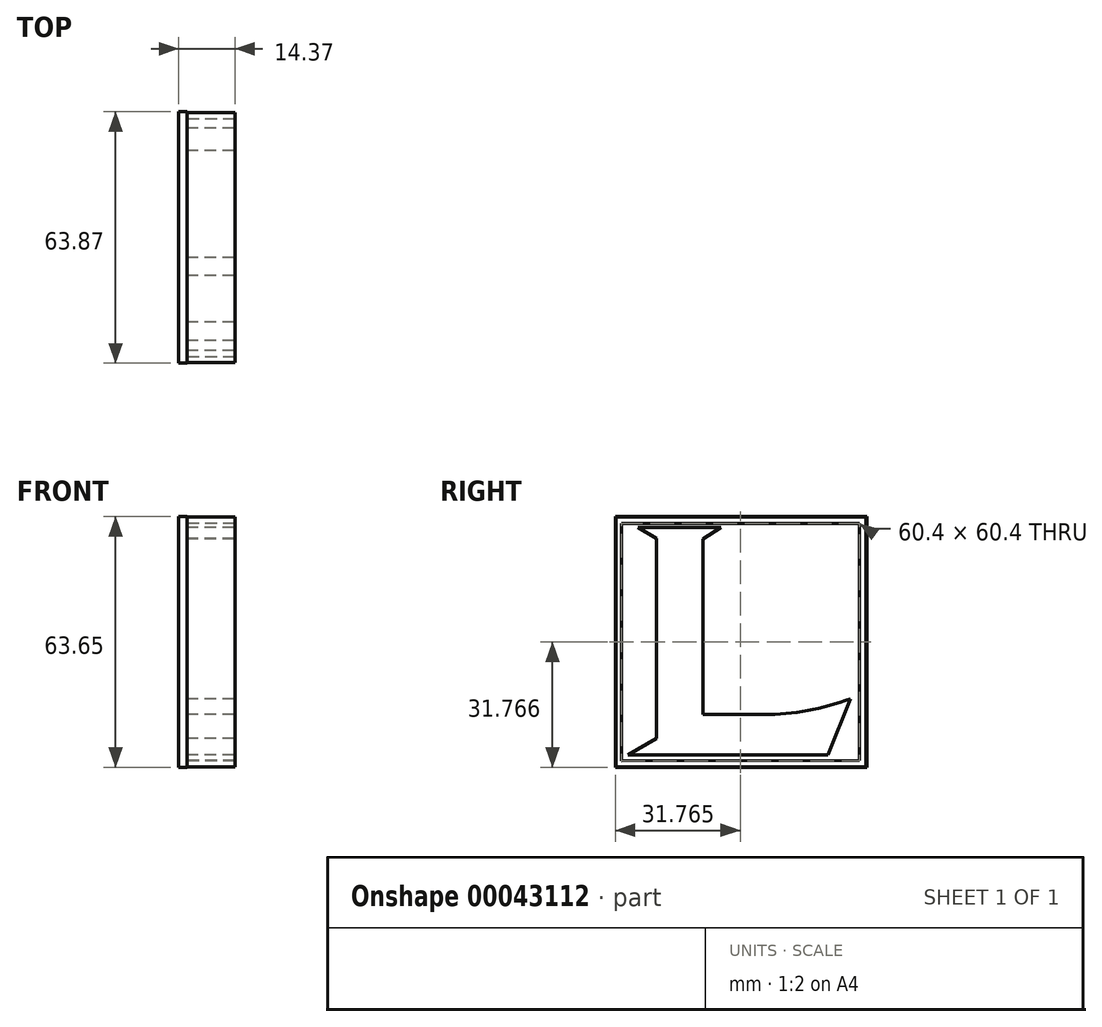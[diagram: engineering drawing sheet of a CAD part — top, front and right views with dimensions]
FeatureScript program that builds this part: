
annotation { "Feature Type Name" : "Feature", "Feature Type Description" : "" }
export const myFeature = defineFeature(function(context is Context, id is Id, definition is map)
    precondition{}
    {
        {
            var Q0;
            Q0=qCreatedBy(makeId("Right.planeOp"),FACE);
            var sketch = newSketch(context, id + "F0", { "sketchPlane" : qUnion([Q0])});
            skLineSegment(sketch, "E0", {"start": v(-7.24, 0) * mm, "end": v(43.56, 0) * mm});
            skLineSegment(sketch, "E1", {"start": v(-7.24, 0) * mm, "end": v(0, 4.13) * mm});
            skLineSegment(sketch, "E2", {"start": v(0, 4.13) * mm, "end": v(0, 54.93) * mm});
            skLineSegment(sketch, "E3", {"start": v(0, 54.93) * mm, "end": v(-4.62, 57.82) * mm});
            skLineSegment(sketch, "E4", {"start": v(-4.62, 57.82) * mm, "end": v(16.37, 57.82) * mm});
            skLineSegment(sketch, "E5", {"start": v(16.37, 57.82) * mm, "end": v(11.85, 54.9) * mm});
            skLineSegment(sketch, "E6", {"start": v(11.85, 54.9) * mm, "end": v(11.85, 10.25) * mm});
            skLineSegment(sketch, "E7", {"start": v(11.85, 10.25) * mm, "end": v(27.27, 10.25) * mm});
            skArc(sketch, "E8", {"start": v(27.27, 10.25) * mm, "mid": v(38.48, 11.25) * mm, "end": v(49.33, 14.23) * mm});
            skLineSegment(sketch, "E9", {"start": v(49.33, 14.23) * mm, "end": v(43.56, 0) * mm});
            skLineSegment(sketch, "E10", {"start": v(-4.62, 57.82) * mm, "end": v(-32.7, 57.82) * mm, "construction": true});
            skLineSegment(sketch, "E11", {"start": v(-32.7, 57.82) * mm, "end": v(-32.7, 0) * mm, "construction": true});
            skLineSegment(sketch, "E12", {"start": v(49.33, 14.23) * mm, "end": v(49.33, -22.32) * mm, "construction": true});
            skLineSegment(sketch, "E13", {"start": v(-7.24, 0) * mm, "end": v(-7.24, -22.1) * mm, "construction": true});
            skLineSegment(sketch, "E14", {"start": v(-7.24, -22.1) * mm, "end": v(49.33, -22.32) * mm, "construction": true});
            skSolve(sketch);
        }
        {
            var Q0;
            Q0=makeQuery(id+"F0.imprint","IMPRINT",FACE,{"disambiguationData":[TD([[makeQuery(id+"F0.imprint","IMPRINT",EDGE,{"derivedFrom":sQuery(id+"F0.wireOp",EDGE,"E0")}),1.0]])]});
            extrude(context, id + "F1", {"entities" : qUnion([Q0]), "depth" : 12.06 * mm});
        }
        {
            var Q0;
            Q0=qCreatedBy(makeId("Right.planeOp"),FACE);
            var sketch = newSketch(context, id + "F2", { "sketchPlane" : qUnion([Q0])});
            skLineSegment(sketch, "E15", {"start": v(-10.25, -3.03) * mm, "end": v(53.25, -3.03) * mm});
            skLineSegment(sketch, "E16", {"start": v(53.25, -3.03) * mm, "end": v(53.25, 60.47) * mm});
            skLineSegment(sketch, "E17", {"start": v(53.25, 60.47) * mm, "end": v(-10.25, 60.47) * mm});
            skLineSegment(sketch, "E18", {"start": v(-10.25, 60.47) * mm, "end": v(-10.25, -3.03) * mm});
            skLineSegment(sketch, "E19", {"start": v(-8.85, -1.59) * mm, "end": v(-8.85, 58.82) * mm});
            skLineSegment(sketch, "E20", {"start": v(-8.85, 58.82) * mm, "end": v(51.56, 58.82) * mm});
            skLineSegment(sketch, "E21", {"start": v(51.56, 58.82) * mm, "end": v(51.56, -1.42) * mm});
            skLineSegment(sketch, "E22", {"start": v(51.56, -1.42) * mm, "end": v(-8.85, -1.59) * mm});
            skLineSegment(sketch, "E23", {"start": v(-10.25, 60.47) * mm, "end": v(-8.85, 58.82) * mm});
            skLineSegment(sketch, "E24", {"start": v(-8.85, -1.59) * mm, "end": v(-10.25, -3.03) * mm});
            skLineSegment(sketch, "E25", {"start": v(51.56, -1.42) * mm, "end": v(53.25, -3.03) * mm});
            skLineSegment(sketch, "E26", {"start": v(51.56, 58.82) * mm, "end": v(53.25, 60.47) * mm});
            skSolve(sketch);
        }
        {
            var Q0;
            Q0 = qSketchRegion(id + "F2", true);
            extrude(context, id + "F3", {"entities" : qUnion([Q0]), "depth" : 12.24 * mm});
        }
        {
            var Q0;
            Q0=qCreatedBy(makeId("Right.planeOp"),FACE);
            var sketch = newSketch(context, id + "F4", { "sketchPlane" : qUnion([Q0])});
            skLineSegment(sketch, "E27.bottom", {"start": v(-10.4, 60.5) * mm, "end": v(53.46, 60.5) * mm});
            skLineSegment(sketch, "E27.top", {"start": v(-10.4, -3.15) * mm, "end": v(53.46, -3.15) * mm});
            skLineSegment(sketch, "E27.left", {"start": v(-10.4, 60.5) * mm, "end": v(-10.4, -3.15) * mm});
            skLineSegment(sketch, "E27.right", {"start": v(53.46, 60.5) * mm, "end": v(53.46, -3.15) * mm});
            skSolve(sketch);
        }
        {
            var Q0;
            Q0 = qSketchRegion(id + "F4", true);
            extrude(context, id + "F5", {"entities" : qUnion([Q0]), "oppositeDirection" : true, "depth" : 2.13 * mm});
        }
    });
